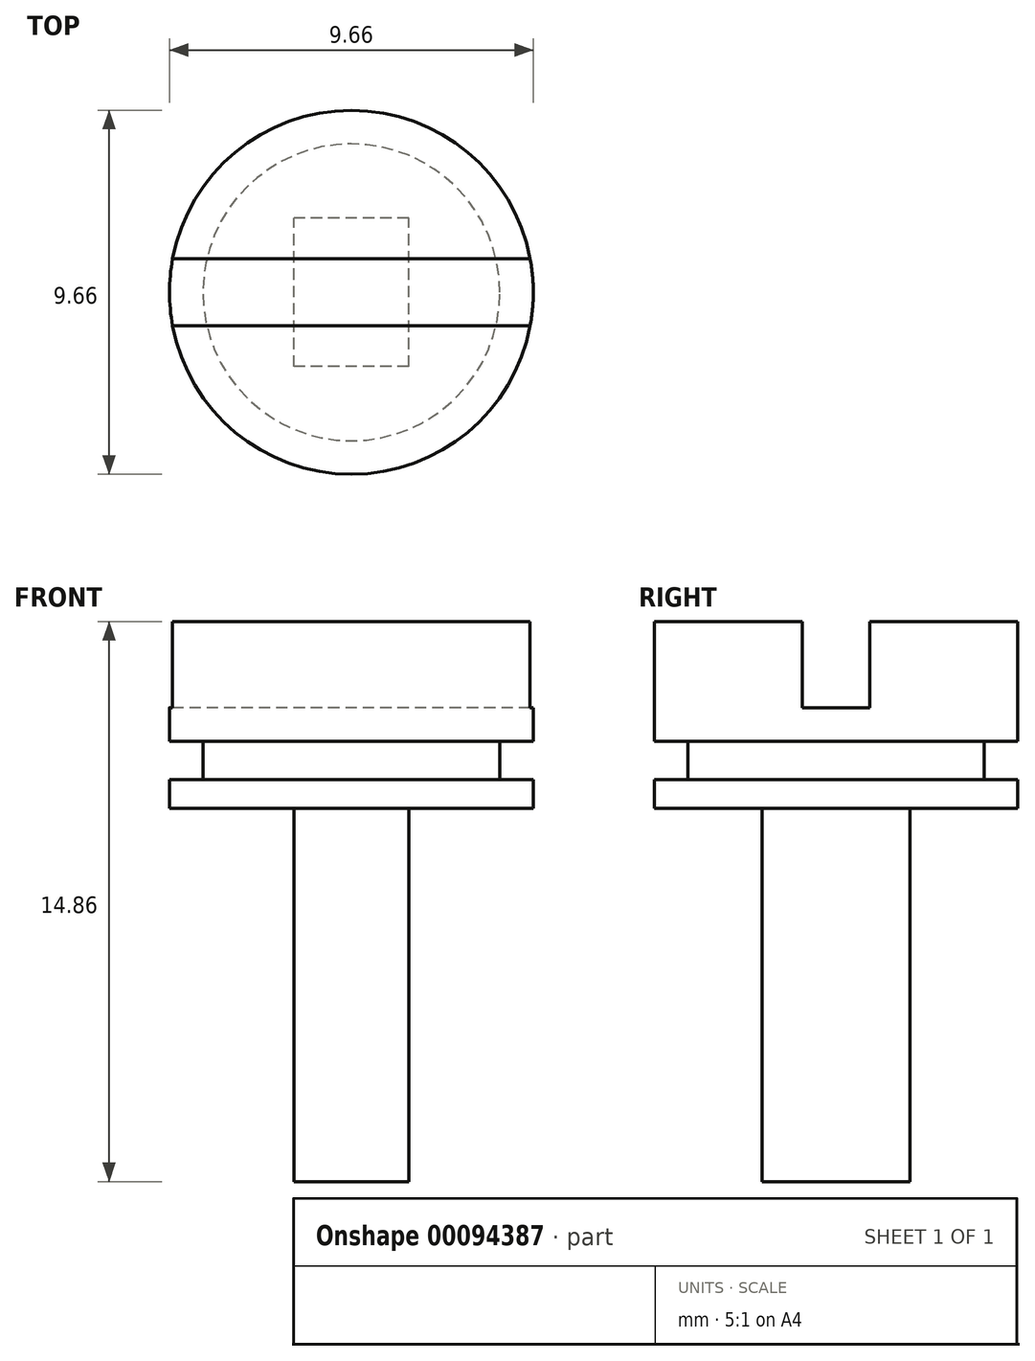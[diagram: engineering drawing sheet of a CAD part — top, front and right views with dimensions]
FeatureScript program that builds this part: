
annotation { "Feature Type Name" : "Feature", "Feature Type Description" : "" }
export const myFeature = defineFeature(function(context is Context, id is Id, definition is map)
    precondition{}
    {
        {
            var Q0;
            Q0=qCreatedBy(makeId("Top.planeOp"),FACE);
            var sketch = newSketch(context, id + "F0", { "sketchPlane" : qUnion([Q0])});
            skCircle(sketch, "E0", {"center": v(0, 0) * mm, "radius": 4.83 * mm});
            skSolve(sketch);
        }
        {
            var Q0;
            Q0 = qSketchRegion(id + "F0", true);
            extrude(context, id + "F1", {"entities" : qUnion([Q0]), "oppositeDirection" : true, "depth" : 3.17 * mm});
        }
        {
            var Q0;
            Q0=makeQuery(id+"F1.opExtrude","CAP_FACE",FACE,{"disambiguationData":[OSD([sQuery(id+"F0.wireOp",EDGE,"E0")])],"isStart":true});
            var sketch = newSketch(context, id + "F2", { "sketchPlane" : qUnion([Q0])});
            skLineSegment(sketch, "E1.bottom", {"start": v(6, 0.89) * mm, "end": v(-6, 0.89) * mm});
            skLineSegment(sketch, "E1.top", {"start": v(6, -0.89) * mm, "end": v(-6, -0.89) * mm});
            skLineSegment(sketch, "E1.left", {"start": v(6, 0.89) * mm, "end": v(6, -0.89) * mm});
            skLineSegment(sketch, "E1.right", {"start": v(-6, 0.89) * mm, "end": v(-6, -0.89) * mm});
            skPoint(sketch, "E1.middle", {"position": v(0, 0) * mm});
            skSolve(sketch);
        }
        {
            var Q0;
            Q0 = qSketchRegion(id + "F2", true);
            extrude(context, id + "F3", {"entities" : qUnion([Q0]), "operationType" : NewBodyOperationType.REMOVE, "oppositeDirection" : true, "depth" : 2.3 * mm});
        }
        {
            var Q0;
            Q0=makeQuery(id+"F1.opExtrude","CAP_FACE",FACE,{"disambiguationData":[OSD([sQuery(id+"F0.wireOp",EDGE,"E0")])],"isStart":false});
            var sketch = newSketch(context, id + "F4", { "sketchPlane" : qUnion([Q0])});
            skCircle(sketch, "E2", {"center": v(0, 0) * mm, "radius": 3.94 * mm});
            skSolve(sketch);
        }
        {
            var Q0;
            Q0=makeQuery(id+"F4.imprint","IMPRINT",FACE,{"disambiguationData":[TD([[makeQuery(id+"F4.imprint","IMPRINT",EDGE,{"derivedFrom":sQuery(id+"F4.wireOp",EDGE,"E2")}),1.0]])]});
            extrude(context, id + "F5", {"entities" : qUnion([Q0]), "operationType" : NewBodyOperationType.ADD, "depth" : 1.02 * mm});
        }
        {
            var Q0;
            Q0=makeQuery(id+"F5.opExtrude","CAP_FACE",FACE,{"disambiguationData":[OSD([sQuery(id+"F4.wireOp",EDGE,"E2")])],"isStart":false});
            var sketch = newSketch(context, id + "F6", { "sketchPlane" : qUnion([Q0])});
            skCircle(sketch, "E3", {"center": v(0, 0) * mm, "radius": 4.83 * mm});
            skSolve(sketch);
        }
        {
            var Q0;
            Q0 = qSketchRegion(id + "F6", true);
            extrude(context, id + "F7", {"entities" : qUnion([Q0]), "operationType" : NewBodyOperationType.ADD, "depth" : 0.76 * mm});
        }
        {
            var Q0;
            Q0=makeQuery(id+"F7.opExtrude","CAP_FACE",FACE,{"disambiguationData":[OSD([sQuery(id+"F6.wireOp",EDGE,"E3")])],"isStart":false});
            var sketch = newSketch(context, id + "F8", { "sketchPlane" : qUnion([Q0])});
            skLineSegment(sketch, "E4.bottom", {"start": v(1.52, 1.97) * mm, "end": v(-1.52, 1.97) * mm});
            skLineSegment(sketch, "E4.top", {"start": v(1.52, -1.97) * mm, "end": v(-1.52, -1.97) * mm});
            skLineSegment(sketch, "E4.left", {"start": v(1.52, 1.97) * mm, "end": v(1.52, -1.97) * mm});
            skLineSegment(sketch, "E4.right", {"start": v(-1.52, 1.97) * mm, "end": v(-1.52, -1.97) * mm});
            skPoint(sketch, "E4.middle", {"position": v(0, 0) * mm});
            skSolve(sketch);
        }
        {
            var Q0;
            Q0 = qSketchRegion(id + "F8", true);
            extrude(context, id + "F9", {"entities" : qUnion([Q0]), "operationType" : NewBodyOperationType.ADD, "depth" : 9.9 * mm});
        }
        {
            var Q0;
            Q0=qCreatedBy(makeId("Front.planeOp"),FACE);
            var sketch = newSketch(context, id + "F10", { "sketchPlane" : qUnion([Q0])});
            skLineSegment(sketch, "E5.bottom", {"start": v(-0.89, -12.2) * mm, "end": v(0.89, -12.2) * mm});
            skLineSegment(sketch, "E5.top", {"start": v(-1.52, -14.86) * mm, "end": v(1.52, -14.86) * mm});
            skLineSegment(sketch, "E5.left", {"start": v(-1.52, -12.83) * mm, "end": v(-1.52, -14.86) * mm});
            skLineSegment(sketch, "E5.right", {"start": v(1.52, -12.83) * mm, "end": v(1.52, -14.86) * mm});
            skPoint(sketch, "E6.visualSharp", {"position": v(-1.52, -12.2) * mm});
            skArc(sketch, "E6.filletArc", {"start": v(-0.89, -12.2) * mm, "mid": v(-1.34, -12.38) * mm, "end": v(-1.52, -12.83) * mm});
            skPoint(sketch, "E7.visualSharp", {"position": v(1.52, -12.2) * mm});
            skArc(sketch, "E7.filletArc", {"start": v(1.52, -12.83) * mm, "mid": v(1.34, -12.38) * mm, "end": v(0.89, -12.2) * mm});
            skSolve(sketch);
        }
        {
            var Q0;
            Q0=sQuery(id+"F10.wireOp",EDGE,"E5.top");
            var Q1;
            Q1=sQuery(id+"F10.wireOp",EDGE,"E5.left");
            var Q2;
            Q2=sQuery(id+"F10.wireOp",EDGE,"E6.filletArc");
            var Q3;
            Q3=sQuery(id+"F10.wireOp",EDGE,"E5.bottom");
            var Q4;
            Q4=sQuery(id+"F10.wireOp",EDGE,"E7.filletArc");
            var Q5;
            Q5=sQuery(id+"F10.wireOp",EDGE,"E5.right");
            extrude(context, id + "F11", {"bodyType" : ToolBodyType.SURFACE, "surfaceEntities" : qUnion([Q0, Q1, Q2, Q3, Q4, Q5]), "endBound" : BoundingType.SYMMETRIC, "depth" : 6.22 * mm});
        }
    });
